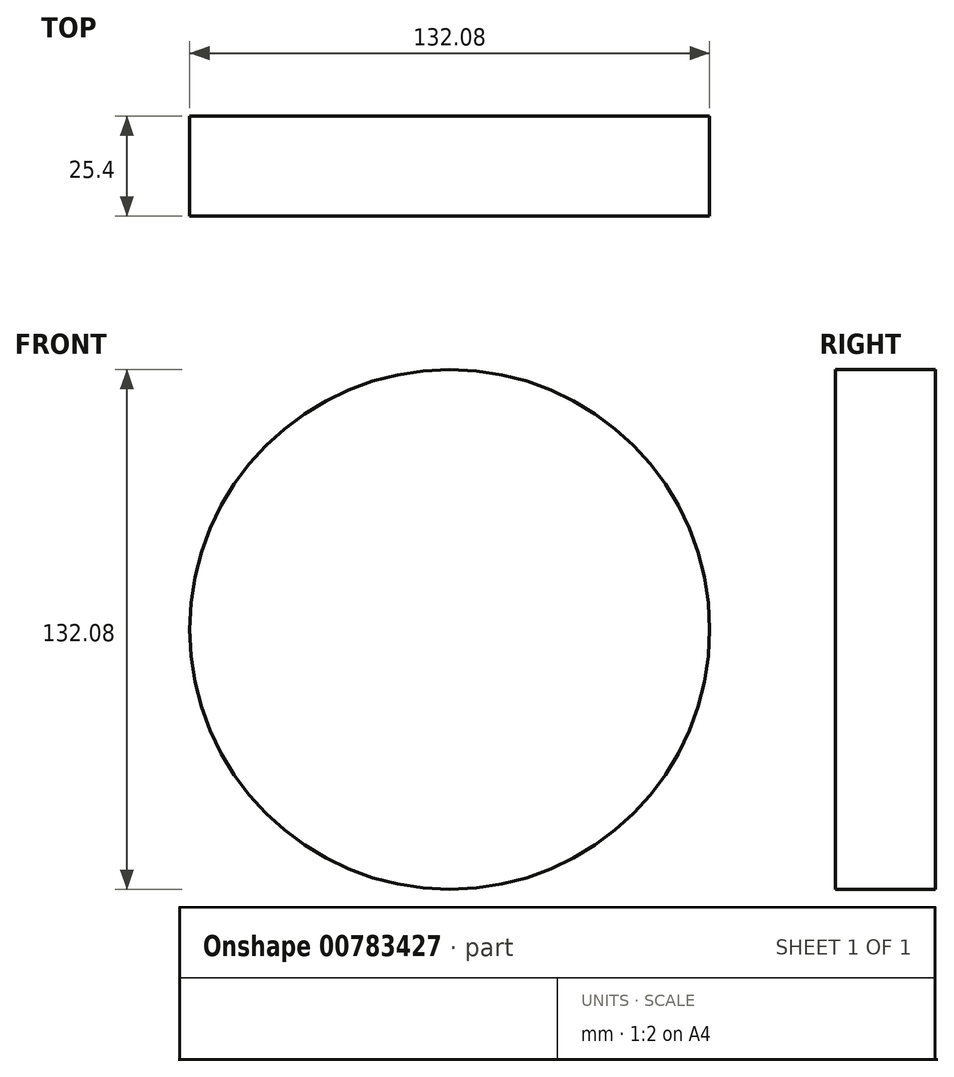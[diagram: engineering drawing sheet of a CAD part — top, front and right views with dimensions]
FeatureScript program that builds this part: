
annotation { "Feature Type Name" : "Feature", "Feature Type Description" : "" }
export const myFeature = defineFeature(function(context is Context, id is Id, definition is map)
    precondition{}
    {
        {
            var Q0;
            Q0=qCreatedBy(makeId("Front.planeOp"),FACE);
            var sketch = newSketch(context, id + "F0", { "sketchPlane" : qUnion([Q0])});
            skCircle(sketch, "E0", {"center": v(0, 0) * mm, "radius": 66.04 * mm});
            skSolve(sketch);
        }
        {
            var Q0;
            Q0=makeQuery(id+"F0.imprint","IMPRINT",FACE,{"disambiguationData":[TD([[makeQuery(id+"F0.imprint","IMPRINT",EDGE,{"derivedFrom":sQuery(id+"F0.wireOp",EDGE,"E0")}),1.0]])]});
            extrude(context, id + "F1", {"entities" : qUnion([Q0]), "depth" : 25.4 * mm, "offsetDistance" : 25.4 * mm});
        }
    });
